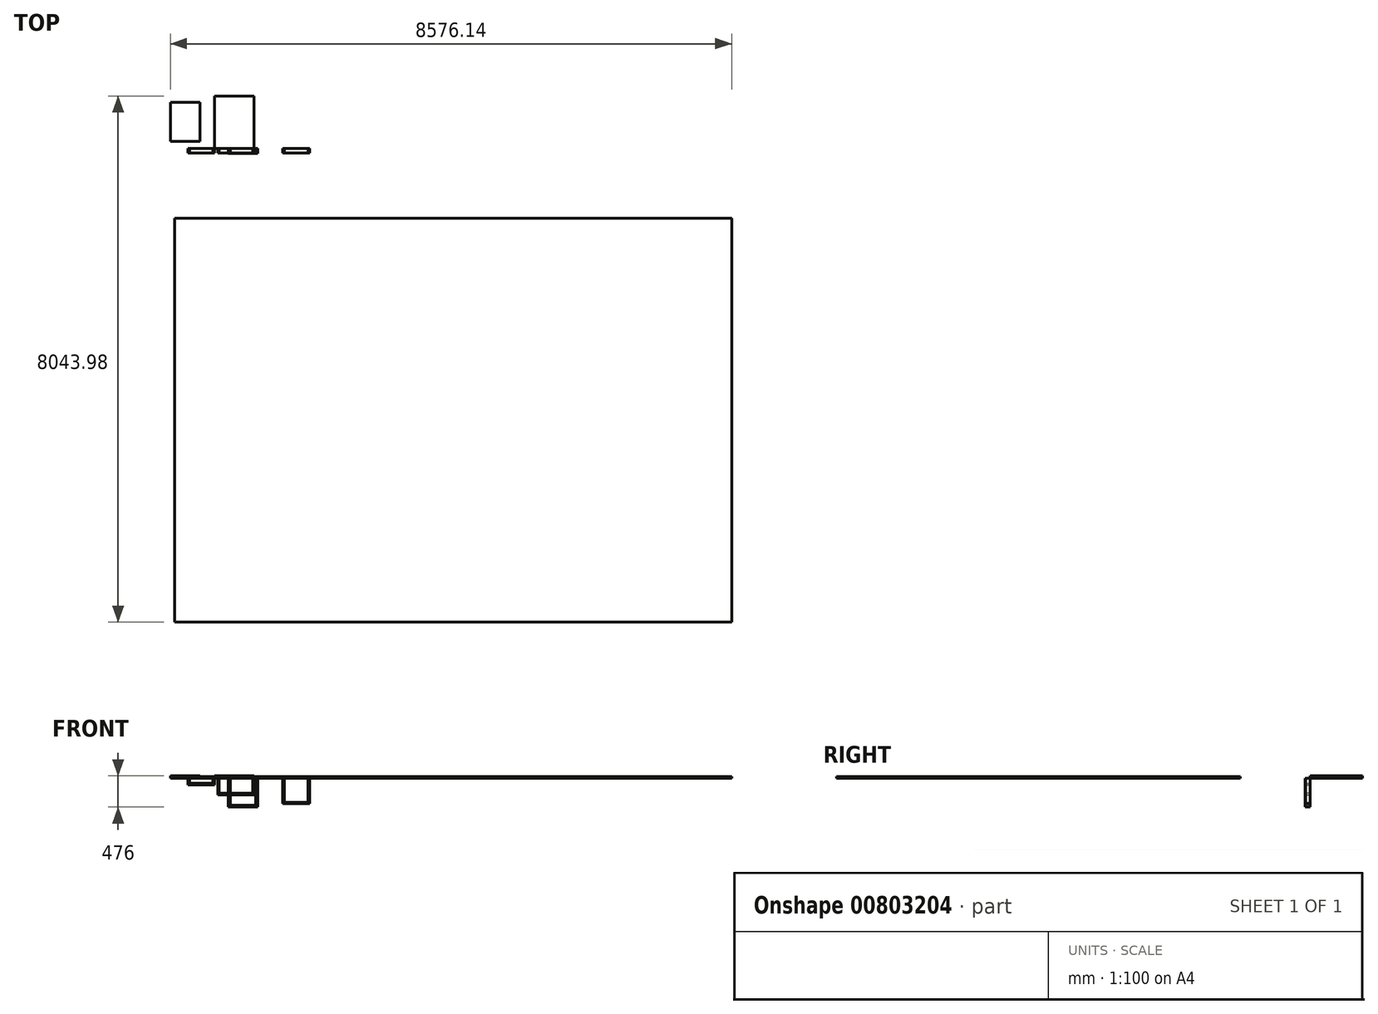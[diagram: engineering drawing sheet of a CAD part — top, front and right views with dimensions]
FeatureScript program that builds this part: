
annotation { "Feature Type Name" : "Feature", "Feature Type Description" : "" }
export const myFeature = defineFeature(function(context is Context, id is Id, definition is map)
    precondition{}
    {
        {
            var Q0;
            Q0=qCreatedBy(makeId("Top.planeOp"),FACE);
            var sketch = newSketch(context, id + "F0", { "sketchPlane" : qUnion([Q0])});
            skLineSegment(sketch, "E0.bottom", {"start": v(0, 0) * mm, "end": v(600, 0) * mm});
            skLineSegment(sketch, "E0.top", {"start": v(0, 800) * mm, "end": v(600, 800) * mm});
            skLineSegment(sketch, "E0.left", {"start": v(0, 0) * mm, "end": v(0, 800) * mm});
            skLineSegment(sketch, "E0.right", {"start": v(600, 0) * mm, "end": v(600, 800) * mm});
            skSolve(sketch);
        }
        {
            var Q0;
            Q0 = qSketchRegion(id + "F0", true);
            extrude(context, id + "F1", {"entities" : qUnion([Q0]), "depth" : 38 * mm, "offsetDistance" : 25 * mm});
        }
        {
            var Q0;
            Q0=qCreatedBy(makeId("Front.planeOp"),FACE);
            var sketch = newSketch(context, id + "F2", { "sketchPlane" : qUnion([Q0])});
            skLineSegment(sketch, "E1", {"start": v(46.26, 0) * mm, "end": v(46.26, -250) * mm});
            skLineSegment(sketch, "E2", {"start": v(46.26, -250) * mm, "end": v(606.26, -250) * mm});
            skLineSegment(sketch, "E3", {"start": v(606.26, -250) * mm, "end": v(606.26, 0) * mm});
            skLineSegment(sketch, "E4", {"start": v(606.26, 0) * mm, "end": v(581.26, 0) * mm});
            skLineSegment(sketch, "E5", {"start": v(581.26, 0) * mm, "end": v(581.26, -225) * mm});
            skLineSegment(sketch, "E6", {"start": v(581.26, -225) * mm, "end": v(71.26, -225) * mm});
            skLineSegment(sketch, "E7", {"start": v(71.26, -225) * mm, "end": v(71.26, 0) * mm});
            skLineSegment(sketch, "E8", {"start": v(71.26, 0) * mm, "end": v(46.26, 0) * mm});
            skSolve(sketch);
        }
        {
            var Q0;
            Q0=makeQuery(id+"F2.imprint","IMPRINT",FACE,{"disambiguationData":[TD([[makeQuery(id+"F2.imprint","IMPRINT",EDGE,{"derivedFrom":sQuery(id+"F2.wireOp",EDGE,"E1")}),1.0]])]});
            extrude(context, id + "F3", {"entities" : qUnion([Q0]), "depth" : 70 * mm, "offsetDistance" : 25 * mm});
        }
        {
            var Q0;
            Q0=qCreatedBy(makeId("Front.planeOp"),FACE);
            var sketch = newSketch(context, id + "F4", { "sketchPlane" : qUnion([Q0])});
            skLineSegment(sketch, "E9", {"start": v(0, 0) * mm, "end": v(0, -100) * mm});
            skLineSegment(sketch, "E10", {"start": v(0, -100) * mm, "end": v(-410, -100) * mm});
            skLineSegment(sketch, "E11", {"start": v(-410, -100) * mm, "end": v(-410, 0) * mm});
            skLineSegment(sketch, "E12", {"start": v(-410, 0) * mm, "end": v(-385, 0) * mm});
            skLineSegment(sketch, "E13", {"start": v(-385, 0) * mm, "end": v(-385, -75) * mm});
            skLineSegment(sketch, "E14", {"start": v(-385, -75) * mm, "end": v(-25, -75) * mm});
            skLineSegment(sketch, "E15", {"start": v(-25, -75) * mm, "end": v(-25, 0) * mm});
            skLineSegment(sketch, "E16", {"start": v(-25, 0) * mm, "end": v(0, 0) * mm});
            skSolve(sketch);
        }
        {
            var Q0;
            Q0=makeQuery(id+"F4.imprint","IMPRINT",FACE,{"disambiguationData":[TD([[makeQuery(id+"F4.imprint","IMPRINT",EDGE,{"derivedFrom":sQuery(id+"F4.wireOp",EDGE,"E9")}),-1.0]])]});
            extrude(context, id + "F5", {"entities" : qUnion([Q0]), "depth" : 70 * mm, "offsetDistance" : 25 * mm});
        }
        {
            var Q0;
            Q0=qCreatedBy(makeId("Front.planeOp"),FACE);
            var sketch = newSketch(context, id + "F6", { "sketchPlane" : qUnion([Q0])});
            skLineSegment(sketch, "E17", {"start": v(207.22, 0) * mm, "end": v(207.22, -438) * mm});
            skLineSegment(sketch, "E18", {"start": v(207.22, -438) * mm, "end": v(657.22, -438) * mm});
            skLineSegment(sketch, "E19", {"start": v(657.22, -438) * mm, "end": v(657.22, 0) * mm});
            skLineSegment(sketch, "E20", {"start": v(657.22, 0) * mm, "end": v(627.22, 0) * mm});
            skLineSegment(sketch, "E21", {"start": v(627.22, 0) * mm, "end": v(627.22, -408) * mm});
            skLineSegment(sketch, "E22", {"start": v(627.22, -408) * mm, "end": v(237.22, -408) * mm});
            skLineSegment(sketch, "E23", {"start": v(237.22, -408) * mm, "end": v(237.22, 0) * mm});
            skLineSegment(sketch, "E24", {"start": v(237.22, 0) * mm, "end": v(207.22, 0) * mm});
            skSolve(sketch);
        }
        {
            var Q0;
            Q0 = qSketchRegion(id + "F6", true);
            extrude(context, id + "F7", {"entities" : qUnion([Q0]), "operationType" : NewBodyOperationType.ADD, "depth" : 80 * mm, "offsetDistance" : 25 * mm});
        }
        {
            var Q0;
            Q0=qCreatedBy(makeId("Front.planeOp"),FACE);
            var sketch = newSketch(context, id + "F8", { "sketchPlane" : qUnion([Q0])});
            skLineSegment(sketch, "E25", {"start": v(1042.06, 0) * mm, "end": v(1042.06, -388) * mm});
            skLineSegment(sketch, "E26", {"start": v(1042.06, -388) * mm, "end": v(1452.06, -388) * mm});
            skLineSegment(sketch, "E27", {"start": v(1452.06, -388) * mm, "end": v(1452.06, 0) * mm});
            skLineSegment(sketch, "E28", {"start": v(1452.06, 0) * mm, "end": v(1427.06, 0) * mm});
            skLineSegment(sketch, "E29", {"start": v(1427.06, 0) * mm, "end": v(1427.06, -363) * mm});
            skLineSegment(sketch, "E30", {"start": v(1427.06, -363) * mm, "end": v(1067.06, -363) * mm});
            skLineSegment(sketch, "E31", {"start": v(1067.06, -363) * mm, "end": v(1067.06, 0) * mm});
            skLineSegment(sketch, "E32", {"start": v(1067.06, 0) * mm, "end": v(1042.06, 0) * mm});
            skSolve(sketch);
        }
        {
            var Q0;
            Q0 = qSketchRegion(id + "F8", true);
            extrude(context, id + "F9", {"entities" : qUnion([Q0]), "depth" : 70 * mm, "offsetDistance" : 25 * mm});
        }
        {
            var Q0;
            Q0=qCreatedBy(makeId("Top.planeOp"),FACE);
            var sketch = newSketch(context, id + "F10", { "sketchPlane" : qUnion([Q0])});
            skLineSegment(sketch, "E33.bottom", {"start": v(-224.16, 102.81) * mm, "end": v(-674.16, 102.81) * mm});
            skLineSegment(sketch, "E33.top", {"start": v(-224.16, 702.81) * mm, "end": v(-674.16, 702.81) * mm});
            skLineSegment(sketch, "E33.left", {"start": v(-224.16, 102.81) * mm, "end": v(-224.16, 702.81) * mm});
            skLineSegment(sketch, "E33.right", {"start": v(-674.16, 102.81) * mm, "end": v(-674.16, 702.81) * mm});
            skSolve(sketch);
        }
        {
            var Q0;
            Q0=makeQuery(id+"F10.imprint","IMPRINT",FACE,{"disambiguationData":[TD([[makeQuery(id+"F10.imprint","IMPRINT",EDGE,{"derivedFrom":sQuery(id+"F10.wireOp",EDGE,"E33.bottom")}),-1.0]])]});
            extrude(context, id + "F11", {"entities" : qUnion([Q0]), "depth" : 38 * mm, "offsetDistance" : 25 * mm});
        }
        {
            var Q0;
            Q0=qCreatedBy(makeId("Top.planeOp"),FACE);
            var sketch = newSketch(context, id + "F12", { "sketchPlane" : qUnion([Q0])});
            skLineSegment(sketch, "E34.bottom", {"start": v(-613.99, -1067.57) * mm, "end": v(7901.98, -1067.57) * mm});
            skLineSegment(sketch, "E34.top", {"start": v(-613.99, -7243.98) * mm, "end": v(7901.98, -7243.98) * mm});
            skLineSegment(sketch, "E34.left", {"start": v(-613.99, -1067.57) * mm, "end": v(-613.99, -7243.98) * mm});
            skLineSegment(sketch, "E34.right", {"start": v(7901.98, -1067.57) * mm, "end": v(7901.98, -7243.98) * mm});
            skSolve(sketch);
        }
        {
            var Q0;
            Q0=makeQuery(id+"F12.imprint","IMPRINT",FACE,{"disambiguationData":[TD([[makeQuery(id+"F12.imprint","IMPRINT",EDGE,{"derivedFrom":sQuery(id+"F12.wireOp",EDGE,"E34.bottom")}),-1.0]])]});
            extrude(context, id + "F13", {"entities" : qUnion([Q0]), "depth" : 25 * mm, "offsetDistance" : 25 * mm});
        }
    });
